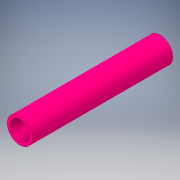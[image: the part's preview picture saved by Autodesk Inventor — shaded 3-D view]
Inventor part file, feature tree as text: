
AUTODESK INVENTOR PART (.ipt)
format: ipt  version: 2018.2 (Build 222227000, 227)  size: 108,544 bytes
history: native  units: in
note: dims shown in document units (in); Inventor stores cm internally (conversion verified against a paired STEP export)
features: extrude x1, sketch x1
ambient origin geometry x8: Origin, YZ Plane, XZ Plane, XY Plane, X Axis, Y Axis, Z Axis, Center Point
bodies: Solid1 (feature_tree)
feature tree (2):
  extrude  "Extrusion1"  Depth=7.25in
  sketch  "Sketch1"  dims[d0=1.315in d1=1.0in d2=7.25in d3=0.0in]
